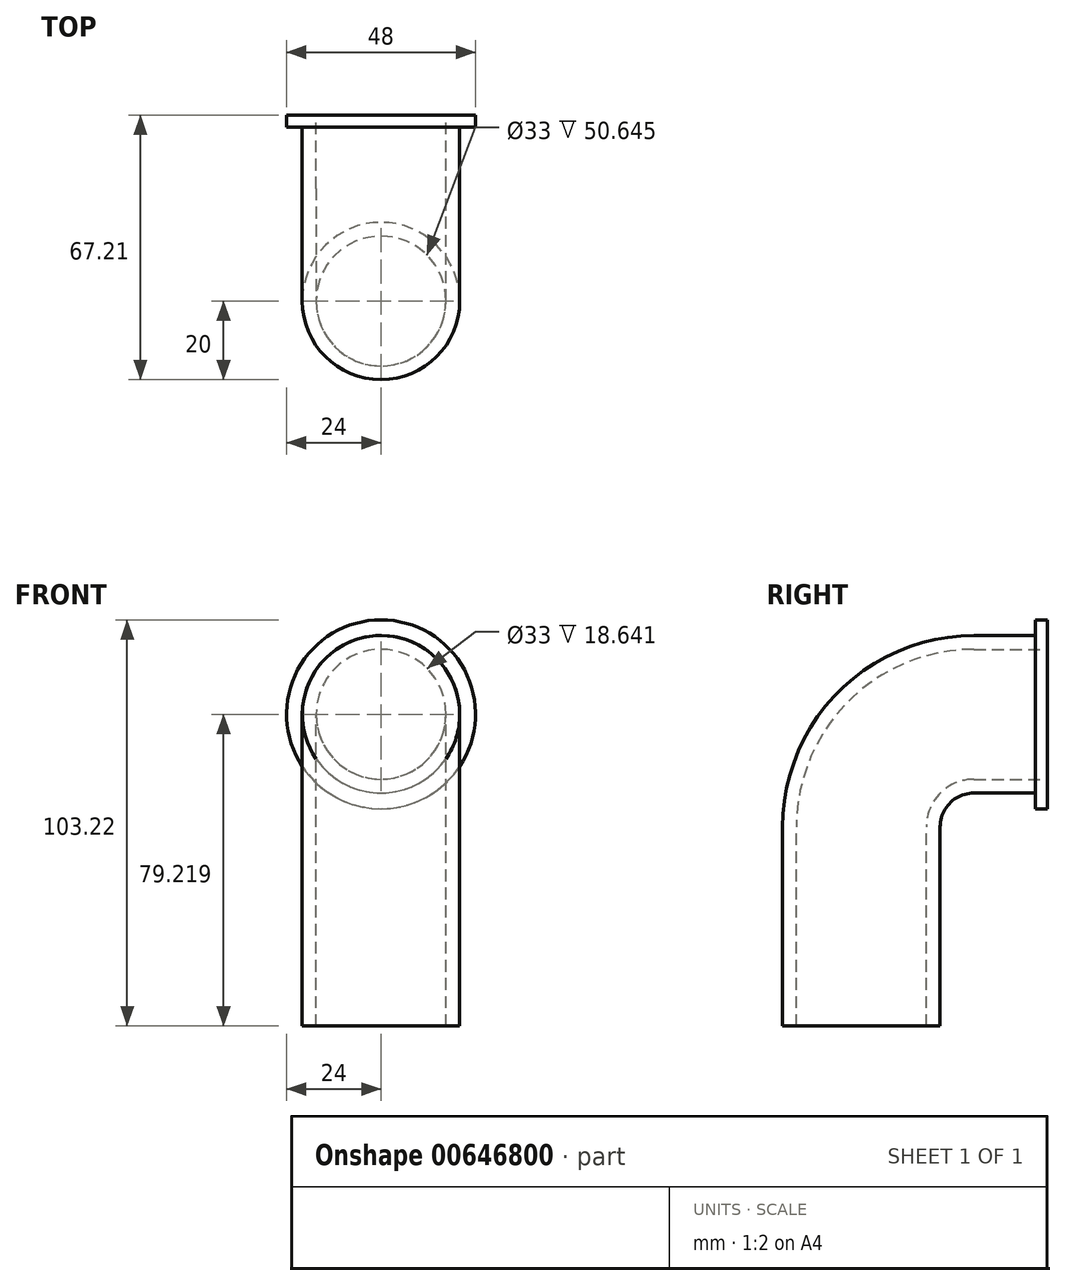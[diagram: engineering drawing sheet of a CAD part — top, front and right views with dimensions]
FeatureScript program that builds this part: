
annotation { "Feature Type Name" : "Feature", "Feature Type Description" : "" }
export const myFeature = defineFeature(function(context is Context, id is Id, definition is map)
    precondition{}
    {
        {
            var Q0;
            Q0=qCreatedBy(makeId("Top.planeOp"),FACE);
            var sketch = newSketch(context, id + "F0", { "sketchPlane" : qUnion([Q0])});
            skCircle(sketch, "E0", {"center": v(0, 0) * mm, "radius": 20 * mm});
            skCircle(sketch, "E1", {"center": v(0, 0) * mm, "radius": 16.5 * mm});
            skSolve(sketch);
        }
        {
            var Q0;
            Q0=qCreatedBy(makeId("Right.planeOp"),FACE);
            var sketch = newSketch(context, id + "F1", { "sketchPlane" : qUnion([Q0])});
            skLineSegment(sketch, "E2", {"start": v(0, 0) * mm, "end": v(0, 50.64) * mm});
            skLineSegment(sketch, "E3.0", {"start": v(-20, 0) * mm, "end": v(20, 0) * mm, "construction": true});
            skArc(sketch, "E4", {"start": v(28.57, 79.22) * mm, "mid": v(8.37, 70.85) * mm, "end": v(0, 50.64) * mm});
            skLineSegment(sketch, "E5", {"start": v(28.57, 79.22) * mm, "end": v(47.21, 79.22) * mm});
            skSolve(sketch);
        }
        {
            var Q0;
            Q0 = qSketchRegion(id + "F0", true);
            var Q1;
            Q1=sQuery(id+"F1.wireOp",EDGE,"E5");
            var Q2;
            Q2=sQuery(id+"F1.wireOp",EDGE,"E4");
            var Q3;
            Q3=sQuery(id+"F1.wireOp",EDGE,"E2");
            sweep(context, id + "F2", {"profiles" : qUnion([Q0]), "path" : qUnion([Q1, Q2, Q3])});
        }
        {
            var Q0;
            Q0=makeQuery(id+"F2.opSweep","CAP_FACE",FACE,{"disambiguationData":[OSD([sQuery(id+"F0.wireOp",EDGE,"E0"),sQuery(id+"F0.wireOp",EDGE,"E1"),sQuery(id+"F1.wireOp",VERTEX,"PvKkmPsP-PI6p-B9wr-gzR6-oJJQiEZwadrO.end")])],"isStart":false});
            var sketch = newSketch(context, id + "F3", { "sketchPlane" : qUnion([Q0])});
            skCircle(sketch, "E6.0", {"center": v(0, 79.22) * mm, "radius": 20 * mm});
            skCircle(sketch, "E7", {"center": v(0, 79.22) * mm, "radius": 24 * mm});
            skSolve(sketch);
        }
        {
            var Q0;
            Q0 = qSketchRegion(id + "F3", true);
            extrude(context, id + "F4", {"entities" : qUnion([Q0]), "operationType" : NewBodyOperationType.ADD, "oppositeDirection" : true, "depth" : 3 * mm, "offsetDistance" : 25 * mm});
        }
    });
